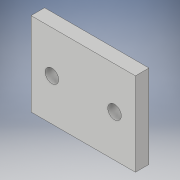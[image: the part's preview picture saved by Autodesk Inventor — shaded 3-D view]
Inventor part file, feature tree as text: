
AUTODESK INVENTOR PART (.ipt)
format: ipt  version: 2018 (Build 220112000, 112)  size: 98,816 bytes
history: native  units: in
note: dims shown in document units (in); Inventor stores cm internally (conversion verified against a paired STEP export)
features: sketch x3, hole x2, extrude x1
ambient origin geometry x8: Origin, YZ Plane, XZ Plane, XY Plane, X Axis, Y Axis, Z Axis, Center Point
bodies: Solid1 (feature_tree)
feature tree (6):
  extrude  "Extrusion1"  Depth=1.5748in
  hole  "Hole1"  [1 undecoded]
  hole  "Hole2"  [1 undecoded]
  sketch  "Sketch1"  dims[d0=1.9685in d1=1.5748in]
  sketch  "Sketch2"  dims[d2=0.2559in d3=0.0in d4=0.2559in]
  sketch  "Sketch3"  dims[d5=0.2559in d6=0.2953in d7=0.1476in d8=0.0984in d9=90.0deg d10=0.3937in d11=0.8108in d12=0.2559in d13=0.2559in d14=0.2953in d15=0.1476in d16=0.0984in d17=90.0deg d18=0.3937in d19=0.8108in]
note: 2 required parameter values undecoded (feature->parameter linkage not recoverable at this tier; creation-order binding heuristic only, values carry confidence <= 0.55)
